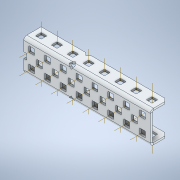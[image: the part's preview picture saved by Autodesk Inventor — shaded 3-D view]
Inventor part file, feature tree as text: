
AUTODESK INVENTOR PART (.ipt)
format: ipt  version: 2020 (Build 240168000, 168)  size: 1,206,272 bytes
history: native  units: in
note: dims shown in document units (in); Inventor stores cm internally (conversion verified against a paired STEP export)
features: other x43, plane x9, pattern_linear x4, split x3, sheet_metal_op x1
ambient origin geometry x8: Origin, YZ Plane, XZ Plane, XY Plane, X Axis, Y Axis, Z Axis, Center Point
bodies: Solid1 (feature_tree)
feature tree (60):
  other  "Work Axis1"
  pattern_linear  "Rectangular Pattern1"  Count1=8 Spacing1=0.5in
  other  "Work Axis72"
  pattern_linear  "Rectangular Pattern2"  Count1=8 Spacing1=0.5in
  pattern_linear  "Rectangular Pattern3"  Count1=8 Spacing1=0.5in
  other  "Work Axis141"
  pattern_linear  "Rectangular Pattern4"  Count1=7 Spacing1=0.5in
  plane  "Work Plane7"
  split  "Split1"
  plane  "Work Plane8"
  split  "Split2"
  plane  "Work Plane9"
  split  "Split3"
  plane  "Work Plane1"
  plane  "Work Plane2"
  other  "Work Point1"
  other  "Work Axis2"
  other  "Work Axis3"
  other  "Work Axis4"
  other  "Work Axis5"
  other  "Work Axis6"
  other  "Work Axis7"
  other  "Work Axis8"
  other  "Work Axis36"
  other  "Work Axis37"
  other  "Work Axis38"
  other  "Work Axis39"
  other  "Work Axis40"
  other  "Work Axis41"
  other  "Work Axis42"
  other  "Work Axis43"
  plane  "Work Plane3"
  plane  "Work Plane4"
  other  "Work Point2"
  other  "Work Axis71"
  other  "Work Point3"
  other  "Work Axis73"
  other  "Work Axis74"
  other  "Work Axis75"
  other  "Work Axis76"
  other  "Work Axis77"
  other  "Work Axis78"
  other  "Work Axis79"
  other  "Work Axis107"
  other  "Work Axis108"
  other  "Work Axis109"
  other  "Work Axis110"
  plane  "Work Plane5"
  plane  "Work Plane6"
  other  "Work Point4"
  other  "Work Axis142"
  other  "Work Axis143"
  other  "Work Axis144"
  other  "Work Axis145"
  other  "Work Axis146"
  other  "Work Axis147"
  other  "Work Axis175"
  other  "Work Axis176"
  other  "Work Axis177"
  sheet_metal_op  "Fold1"
